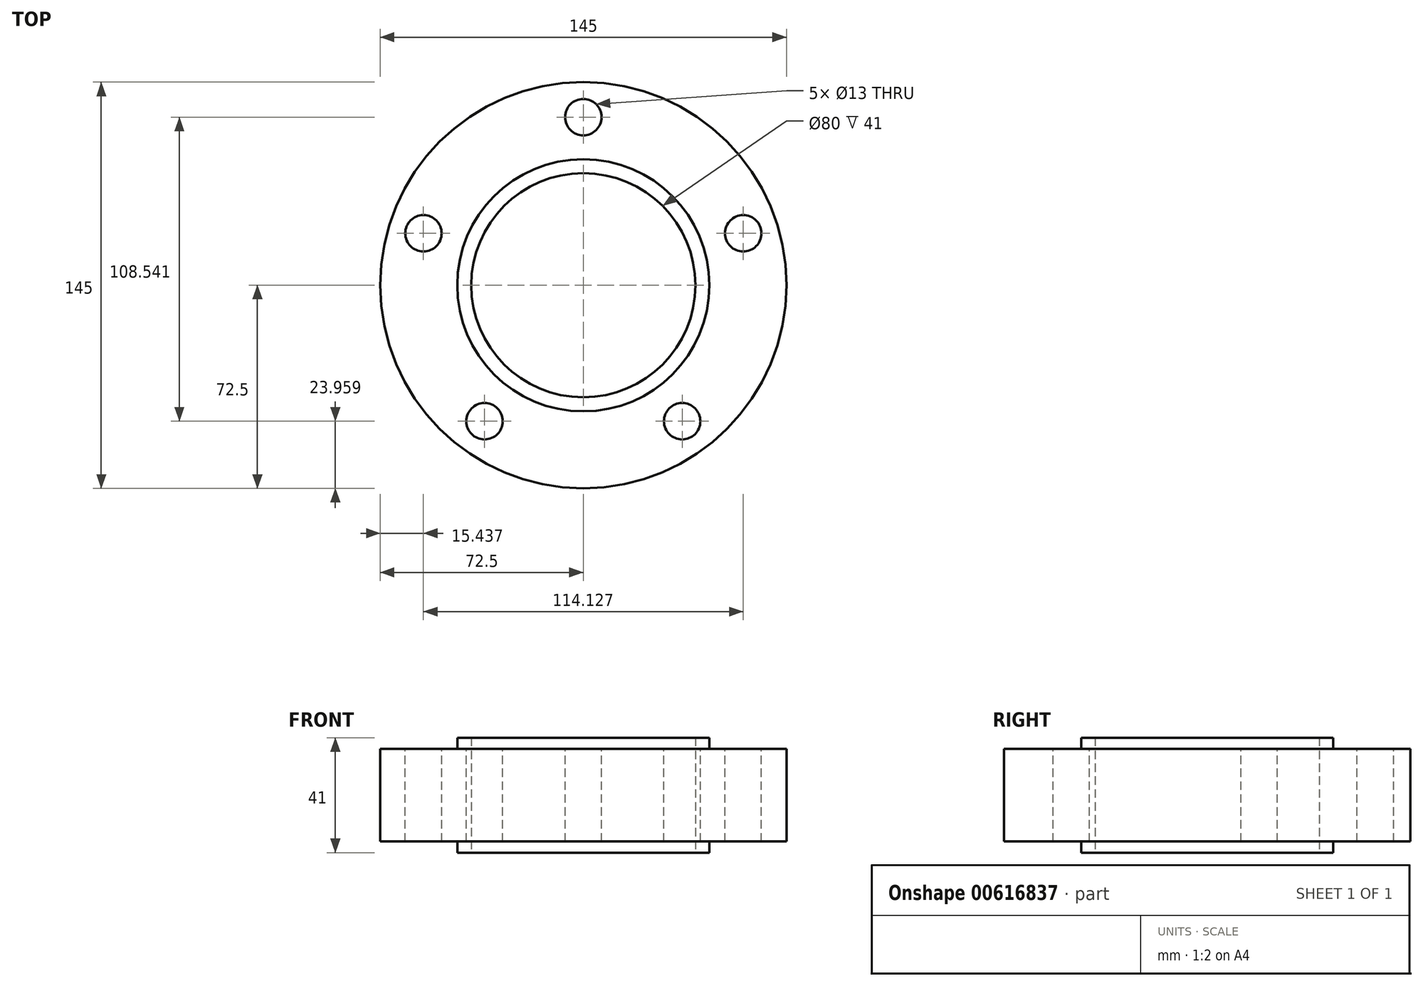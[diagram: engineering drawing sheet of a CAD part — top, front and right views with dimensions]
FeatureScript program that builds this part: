
annotation { "Feature Type Name" : "Feature", "Feature Type Description" : "" }
export const myFeature = defineFeature(function(context is Context, id is Id, definition is map)
    precondition{}
    {
        {
            var Q0;
            Q0=qCreatedBy(makeId("Front.planeOp"),FACE);
            var sketch = newSketch(context, id + "F0", { "sketchPlane" : qUnion([Q0])});
            skLineSegment(sketch, "E0", {"start": v(40, 0) * mm, "end": v(40, 41) * mm});
            skLineSegment(sketch, "E1", {"start": v(40, 41) * mm, "end": v(45, 41) * mm});
            skLineSegment(sketch, "E2", {"start": v(45, 41) * mm, "end": v(45, 37) * mm});
            skLineSegment(sketch, "E3", {"start": v(45, 37) * mm, "end": v(72.5, 37) * mm});
            skLineSegment(sketch, "E4", {"start": v(72.5, 37) * mm, "end": v(72.5, 4) * mm});
            skLineSegment(sketch, "E5", {"start": v(72.5, 4) * mm, "end": v(45, 4) * mm});
            skLineSegment(sketch, "E6", {"start": v(45, 4) * mm, "end": v(45, 0) * mm});
            skLineSegment(sketch, "E7", {"start": v(45, 0) * mm, "end": v(40, 0) * mm});
            skLineSegment(sketch, "E8", {"start": v(0, 0) * mm, "end": v(0, 82.15) * mm, "construction": true});
            skSolve(sketch);
        }
        {
            var Q0;
            Q0=makeQuery(id+"F0.imprint","IMPRINT",FACE,{"disambiguationData":[TD([[makeQuery(id+"F0.imprint","IMPRINT",EDGE,{"derivedFrom":sQuery(id+"F0.wireOp",EDGE,"E0")}),-1.0]])]});
            var Q1;
            Q1=sQuery(id+"F0.wireOp",EDGE,"E8");
            revolve(context, id + "F1", {"surfaceOperationType" : NewSurfaceOperationType.NEW, "entities" : qUnion([Q0]), "axis" : qUnion([Q1]), "revolveType" : RevolveType.FULL});
        }
        {
            var Q0;
            Q0=makeQuery(id+"F1.opRevolve","SWEPT_FACE",FACE,{"disambiguationData":[OSD([sQuery(id+"F0.wireOp",EDGE,"E3")])]});
            var sketch = newSketch(context, id + "F2", { "sketchPlane" : qUnion([Q0])});
            skCircle(sketch, "E9", {"center": v(0, 0) * mm, "radius": 60 * mm, "construction": true});
            skCircle(sketch, "E10", {"center": v(0, 60) * mm, "radius": 6.5 * mm});
            skCircle(sketch, "E11.1.0", {"center": v(-57.06, 18.54) * mm, "radius": 6.5 * mm});
            skCircle(sketch, "E11.2.0", {"center": v(-35.27, -48.54) * mm, "radius": 6.5 * mm});
            skCircle(sketch, "E11.3.0", {"center": v(35.27, -48.54) * mm, "radius": 6.5 * mm});
            skCircle(sketch, "E11.4.0", {"center": v(57.06, 18.54) * mm, "radius": 6.5 * mm});
            skSolve(sketch);
        }
        {
            var Q0;
            Q0 = qSketchRegion(id + "F2", true);
            extrude(context, id + "F3", {"entities" : qUnion([Q0]), "operationType" : NewBodyOperationType.REMOVE, "endBound" : BoundingType.UP_TO_NEXT, "oppositeDirection" : true, "depth" : 25 * mm, "offsetDistance" : 25 * mm});
        }
    });
